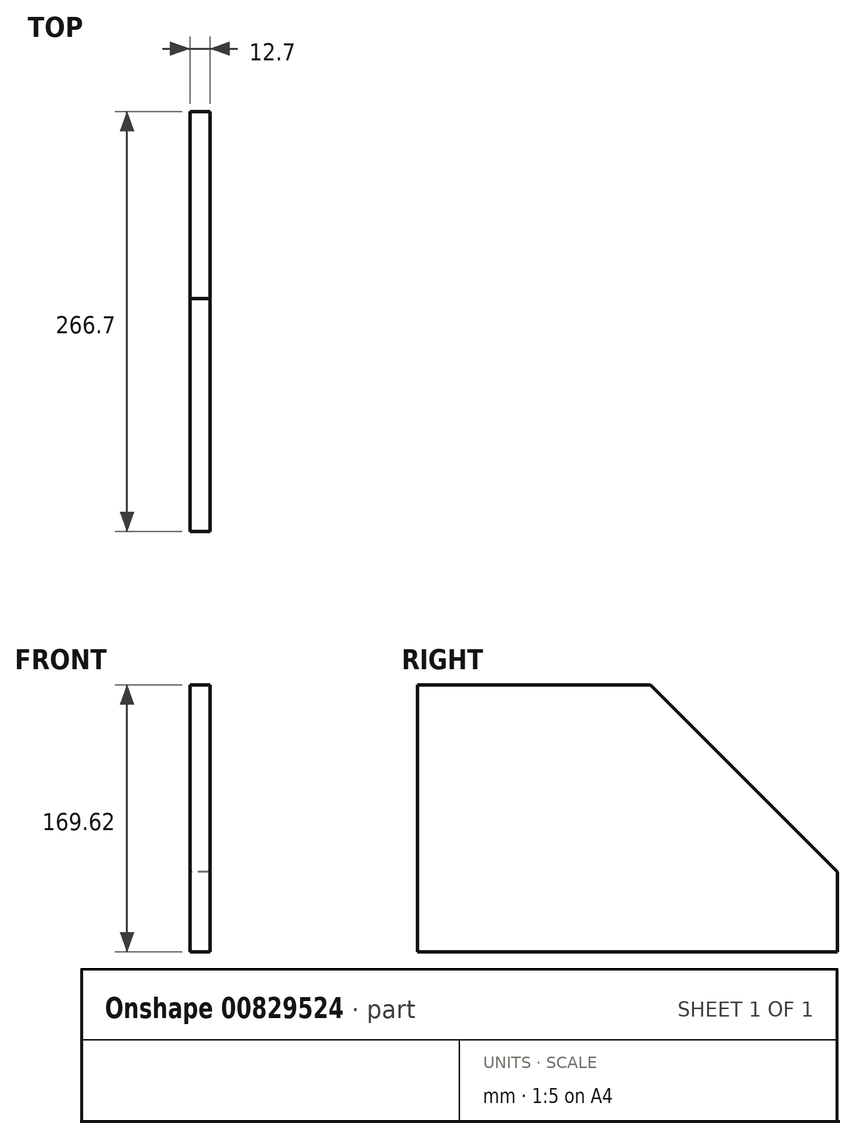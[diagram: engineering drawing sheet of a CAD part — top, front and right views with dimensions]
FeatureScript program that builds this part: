
annotation { "Feature Type Name" : "Feature", "Feature Type Description" : "" }
export const myFeature = defineFeature(function(context is Context, id is Id, definition is map)
    precondition{}
    {
        {
            var Q0;
            Q0=qCreatedBy(makeId("Right.planeOp"),FACE);
            var sketch = newSketch(context, id + "F0", { "sketchPlane" : qUnion([Q0])});
            skLineSegment(sketch, "E0", {"start": v(-109.55, -49.29) * mm, "end": v(157.15, -49.29) * mm});
            skLineSegment(sketch, "E1", {"start": v(157.15, -49.29) * mm, "end": v(157.15, 1.51) * mm});
            skLineSegment(sketch, "E2", {"start": v(-109.55, -49.29) * mm, "end": v(-109.55, 120.33) * mm});
            skLineSegment(sketch, "E3", {"start": v(-109.55, 120.33) * mm, "end": v(38.33, 120.33) * mm});
            skLineSegment(sketch, "E4", {"start": v(38.33, 120.33) * mm, "end": v(157.15, 1.51) * mm});
            skSolve(sketch);
        }
        {
            var Q0;
            Q0 = qSketchRegion(id + "F0", true);
            extrude(context, id + "F1", {"entities" : qUnion([Q0]), "depth" : 12.7 * mm, "offsetDistance" : 25.4 * mm});
        }
    });
